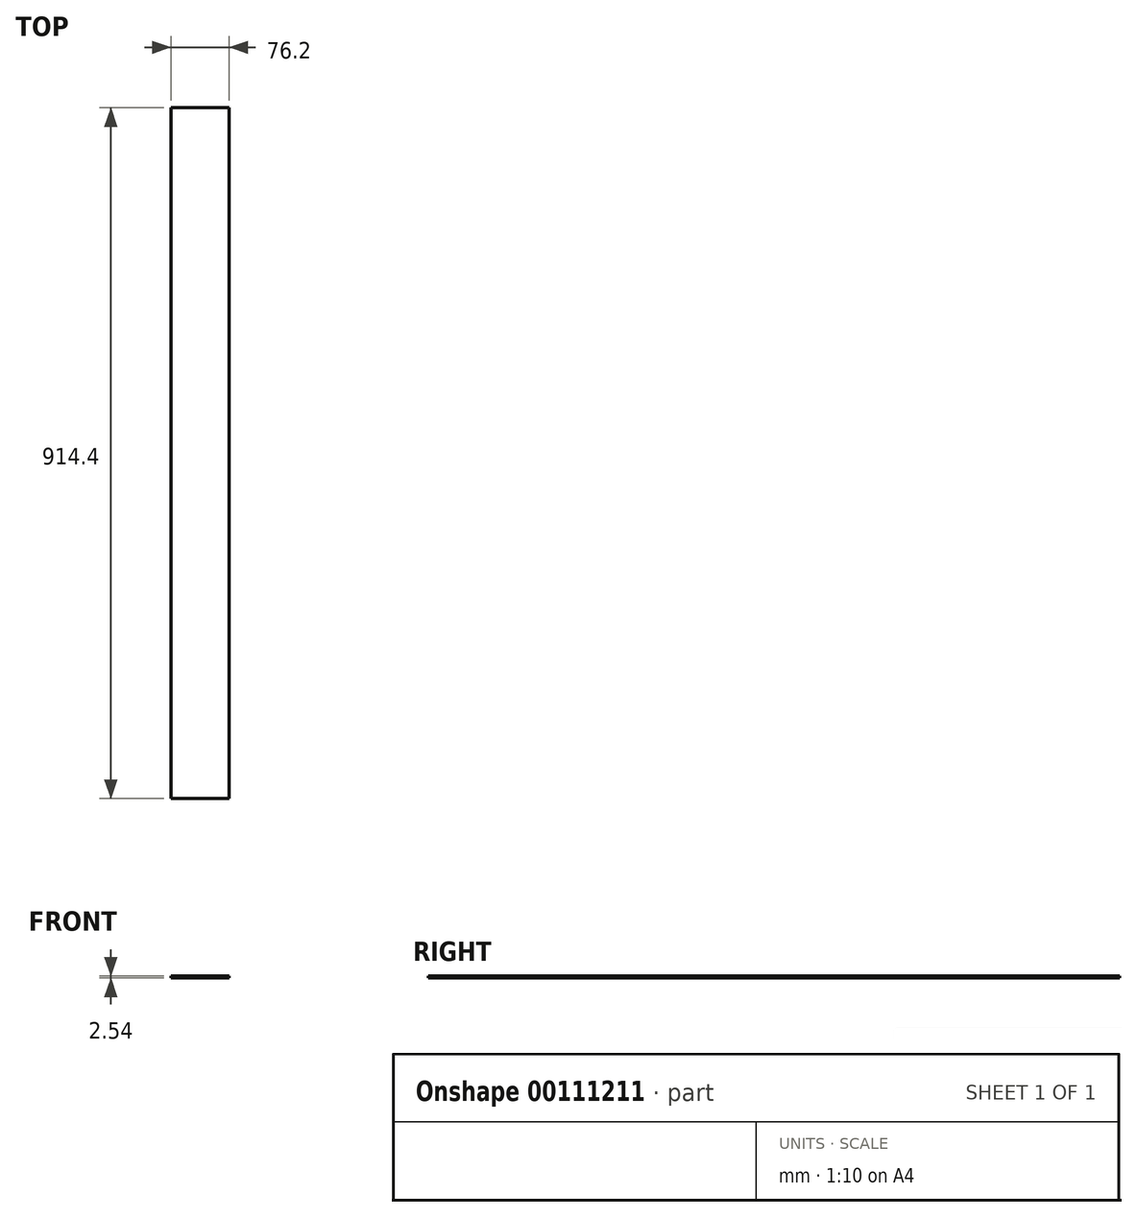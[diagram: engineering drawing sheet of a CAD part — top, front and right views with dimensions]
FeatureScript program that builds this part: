
annotation { "Feature Type Name" : "Feature", "Feature Type Description" : "" }
export const myFeature = defineFeature(function(context is Context, id is Id, definition is map)
    precondition{}
    {
        {
            var Q0;
            Q0=qCreatedBy(makeId("Front.planeOp"),FACE);
            var sketch = newSketch(context, id + "F0", { "sketchPlane" : qUnion([Q0])});
            skLineSegment(sketch, "E0.bottom", {"start": v(38.1, 1.27) * mm, "end": v(-38.1, 1.27) * mm});
            skLineSegment(sketch, "E0.top", {"start": v(38.1, -1.27) * mm, "end": v(-38.1, -1.27) * mm});
            skLineSegment(sketch, "E0.left", {"start": v(38.1, 1.27) * mm, "end": v(38.1, -1.27) * mm});
            skLineSegment(sketch, "E0.right", {"start": v(-38.1, 1.27) * mm, "end": v(-38.1, -1.27) * mm});
            skPoint(sketch, "E0.middle", {"position": v(0, 0) * mm});
            skSolve(sketch);
        }
        {
            var Q0;
            Q0=makeQuery(id+"F0.imprint","IMPRINT",FACE,{"disambiguationData":[TD([[makeQuery(id+"F0.imprint","IMPRINT",EDGE,{"derivedFrom":sQuery(id+"F0.wireOp",EDGE,"E0.bottom")}),1.0]])]});
            extrude(context, id + "F1", {"entities" : qUnion([Q0]), "depth" : 914.4 * mm});
        }
    });
